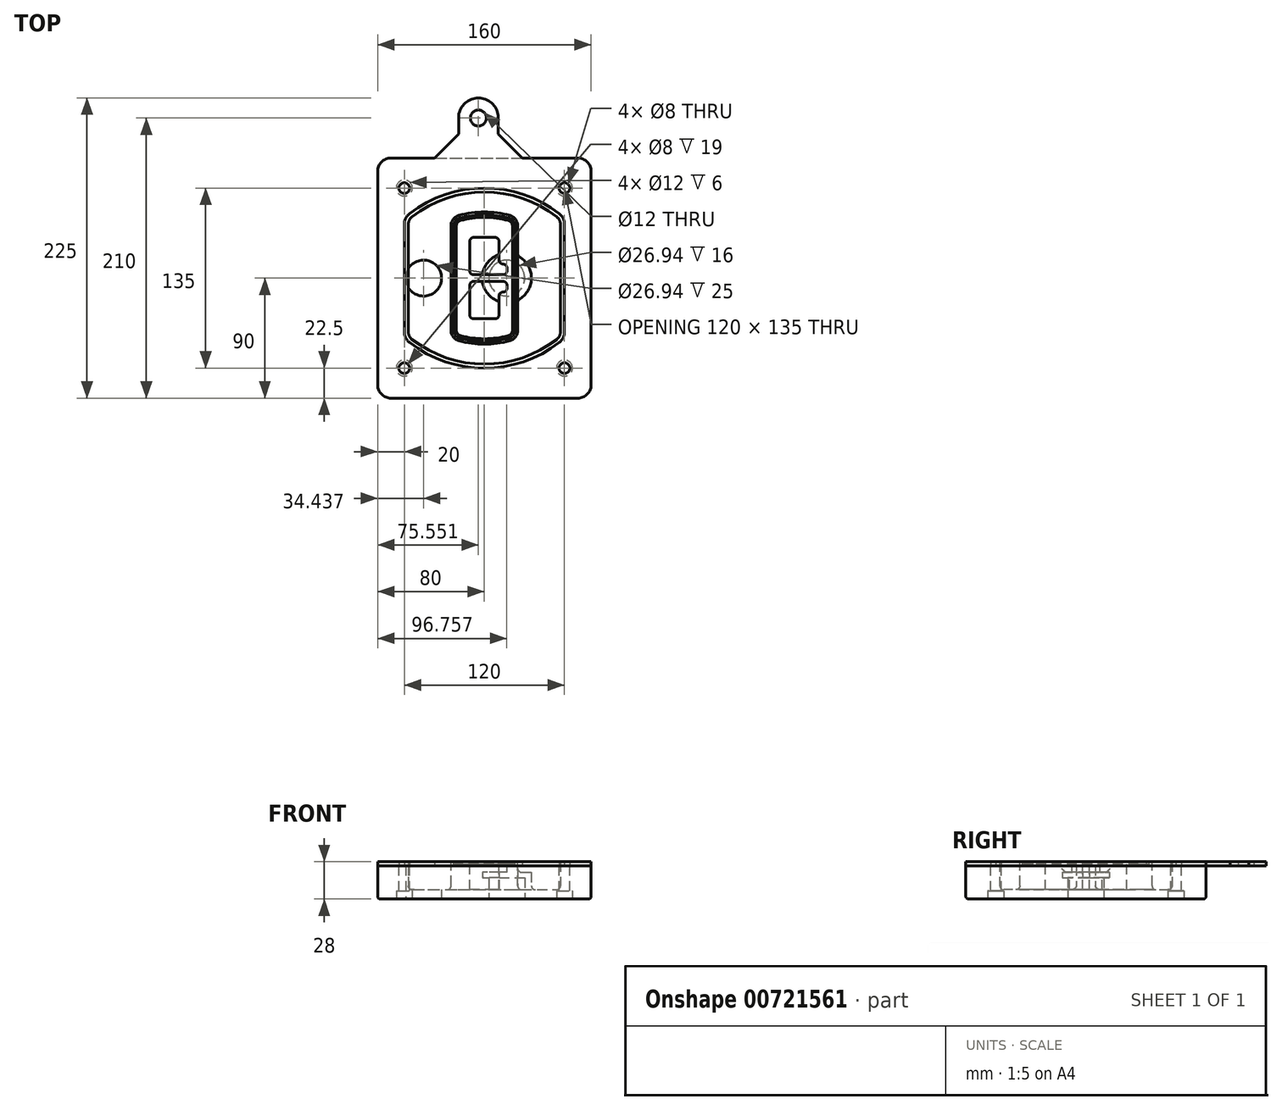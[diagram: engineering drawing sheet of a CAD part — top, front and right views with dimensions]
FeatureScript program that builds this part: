
annotation { "Feature Type Name" : "Feature", "Feature Type Description" : "" }
export const myFeature = defineFeature(function(context is Context, id is Id, definition is map)
    precondition{}
    {
        {
            var Q0;
            Q0=qCreatedBy(makeId("Top.planeOp"),FACE);
            var sketch = newSketch(context, id + "F0", { "sketchPlane" : qUnion([Q0])});
            skPoint(sketch, "E0.rect.middle", {"position": v(0, 0) * mm});
            skLineSegment(sketch, "E1.bottom", {"start": v(-70, -90) * mm, "end": v(70, -90) * mm});
            skLineSegment(sketch, "E1.top", {"start": v(-70, 90) * mm, "end": v(70, 90) * mm});
            skLineSegment(sketch, "E1.left", {"start": v(-80, -80) * mm, "end": v(-80, 80) * mm});
            skLineSegment(sketch, "E1.right", {"start": v(80, -80) * mm, "end": v(80, 80) * mm});
            skLineSegment(sketch, "E2", {"start": v(-80, 90) * mm, "end": v(80, -90) * mm, "construction": true});
            skLineSegment(sketch, "E3", {"start": v(80, 90) * mm, "end": v(-80, -90) * mm, "construction": true});
            skCircle(sketch, "E4", {"center": v(-60, 67.5) * mm, "radius": 4 * mm});
            skCircle(sketch, "E5", {"center": v(60, 67.5) * mm, "radius": 4 * mm});
            skCircle(sketch, "E6", {"center": v(60, -67.5) * mm, "radius": 4 * mm});
            skCircle(sketch, "E7", {"center": v(-60, -67.5) * mm, "radius": 4 * mm});
            skLineSegment(sketch, "E8", {"start": v(-60, 67.5) * mm, "end": v(60, 67.5) * mm, "construction": true});
            skLineSegment(sketch, "E9", {"start": v(60, 67.5) * mm, "end": v(60, -67.5) * mm, "construction": true});
            skLineSegment(sketch, "E10", {"start": v(60, -67.5) * mm, "end": v(-60, -67.5) * mm, "construction": true});
            skLineSegment(sketch, "E11", {"start": v(-60, -67.5) * mm, "end": v(-60, 67.5) * mm, "construction": true});
            skLineSegment(sketch, "E12", {"start": v(-60, 40.3) * mm, "end": v(-60, -40.3) * mm});
            skLineSegment(sketch, "E13", {"start": v(60, 40.3) * mm, "end": v(60, -40.3) * mm});
            skArc(sketch, "E14", {"start": v(56.15, 48.18) * mm, "mid": v(0, 67.5) * mm, "end": v(-56.15, 48.18) * mm});
            skArc(sketch, "E15", {"start": v(-56.15, -48.18) * mm, "mid": v(0, -67.5) * mm, "end": v(56.15, -48.18) * mm});
            skLineSegment(sketch, "E16", {"start": v(-60, 0) * mm, "end": v(60, 0) * mm, "construction": true});
            skPoint(sketch, "E17.visualSharp", {"position": v(-60, -45) * mm});
            skArc(sketch, "E17.filletArc", {"start": v(-60, -40.3) * mm, "mid": v(-58.99, -44.68) * mm, "end": v(-56.15, -48.18) * mm});
            skPoint(sketch, "E18.visualSharp", {"position": v(-60, 45) * mm});
            skArc(sketch, "E18.filletArc", {"start": v(-56.15, 48.18) * mm, "mid": v(-58.99, 44.68) * mm, "end": v(-60, 40.3) * mm});
            skPoint(sketch, "E19.visualSharp", {"position": v(60, 45) * mm});
            skArc(sketch, "E19.filletArc", {"start": v(60, 40.3) * mm, "mid": v(58.99, 44.68) * mm, "end": v(56.15, 48.18) * mm});
            skPoint(sketch, "E20.visualSharp", {"position": v(60, -45) * mm});
            skArc(sketch, "E20.filletArc", {"start": v(56.15, -48.18) * mm, "mid": v(58.99, -44.68) * mm, "end": v(60, -40.3) * mm});
            skPoint(sketch, "E21.visualSharp", {"position": v(-80, 90) * mm});
            skArc(sketch, "E21.filletArc", {"start": v(-70, 90) * mm, "mid": v(-77.07, 87.07) * mm, "end": v(-80, 80) * mm});
            skPoint(sketch, "E22.visualSharp", {"position": v(80, 90) * mm});
            skArc(sketch, "E22.filletArc", {"start": v(80, 80) * mm, "mid": v(77.07, 87.07) * mm, "end": v(70, 90) * mm});
            skPoint(sketch, "E23.visualSharp", {"position": v(80, -90) * mm});
            skArc(sketch, "E23.filletArc", {"start": v(70, -90) * mm, "mid": v(77.07, -87.07) * mm, "end": v(80, -80) * mm});
            skPoint(sketch, "E24.visualSharp", {"position": v(-80, -90) * mm});
            skArc(sketch, "E24.filletArc", {"start": v(-80, -80) * mm, "mid": v(-77.07, -87.07) * mm, "end": v(-70, -90) * mm});
            skArc(sketch, "E25.0", {"start": v(57, 40.3) * mm, "mid": v(56.3, 43.36) * mm, "end": v(54.3, 45.81) * mm});
            skLineSegment(sketch, "E25.1", {"start": v(57, 40.3) * mm, "end": v(57, -40.3) * mm});
            skArc(sketch, "E25.2", {"start": v(54.3, -45.81) * mm, "mid": v(56.3, -43.36) * mm, "end": v(57, -40.3) * mm});
            skArc(sketch, "E25.3", {"start": v(-54.3, -45.81) * mm, "mid": v(0, -64.5) * mm, "end": v(54.3, -45.81) * mm});
            skArc(sketch, "E25.4", {"start": v(-57, -40.3) * mm, "mid": v(-56.3, -43.36) * mm, "end": v(-54.3, -45.81) * mm});
            skArc(sketch, "E25.5", {"start": v(54.3, 45.81) * mm, "mid": v(0, 64.5) * mm, "end": v(-54.3, 45.81) * mm});
            skLineSegment(sketch, "E25.6", {"start": v(-57, 40.3) * mm, "end": v(-57, -40.3) * mm});
            skArc(sketch, "E25.7", {"start": v(-54.3, 45.81) * mm, "mid": v(-56.3, 43.36) * mm, "end": v(-57, 40.3) * mm});
            skArc(sketch, "E26.0", {"start": v(-58.62, 51.33) * mm, "mid": v(-62.58, 46.43) * mm, "end": v(-64, 40.3) * mm});
            skArc(sketch, "E26.1", {"start": v(58.62, 51.33) * mm, "mid": v(0, 71.5) * mm, "end": v(-58.62, 51.33) * mm});
            skArc(sketch, "E26.2", {"start": v(64, 40.3) * mm, "mid": v(62.58, 46.43) * mm, "end": v(58.62, 51.33) * mm});
            skLineSegment(sketch, "E26.3", {"start": v(64, 40.3) * mm, "end": v(64, -40.3) * mm});
            skArc(sketch, "E26.4", {"start": v(58.62, -51.33) * mm, "mid": v(62.58, -46.43) * mm, "end": v(64, -40.3) * mm});
            skLineSegment(sketch, "E26.5", {"start": v(-64, 40.3) * mm, "end": v(-64, -40.3) * mm});
            skArc(sketch, "E26.6", {"start": v(-58.62, -51.33) * mm, "mid": v(0, -71.5) * mm, "end": v(58.62, -51.33) * mm});
            skArc(sketch, "E26.7", {"start": v(-64, -40.3) * mm, "mid": v(-62.58, -46.43) * mm, "end": v(-58.62, -51.33) * mm});
            skSolve(sketch);
        }
        {
            var Q0;
            Q0=makeQuery(id+"F0.imprint","IMPRINT",FACE,{"disambiguationData":[TD([[makeQuery(id+"F0.imprint","IMPRINT",EDGE,{"derivedFrom":sQuery(id+"F0.wireOp",EDGE,"E1.bottom")}),1.0]])]});
            var Q1;
            Q1=makeQuery(id+"F0.imprint","IMPRINT",FACE,{"disambiguationData":[TD([[makeQuery(id+"F0.imprint","IMPRINT",EDGE,{"derivedFrom":sQuery(id+"F0.wireOp",EDGE,"E12")}),1.0]])]});
            var Q2;
            Q2=makeQuery(id+"F0.imprint","IMPRINT",FACE,{"disambiguationData":[TD([[makeQuery(id+"F0.imprint","IMPRINT",EDGE,{"derivedFrom":sQuery(id+"F0.wireOp",EDGE,"E25.0")}),1.0]])]});
            var Q3;
            Q3=makeQuery(id+"F0.imprint","IMPRINT",FACE,{"disambiguationData":[TD([[makeQuery(id+"F0.imprint","IMPRINT",EDGE,{"derivedFrom":sQuery(id+"F0.wireOp",EDGE,"E12")}),-1.0]])]});
            extrude(context, id + "F1", {"entities" : qUnion([Q0, Q1, Q2, Q3]), "oppositeDirection" : true, "depth" : 25 * mm});
        }
        {
            var Q0;
            Q0=makeQuery(id+"F0.imprint","IMPRINT",FACE,{"disambiguationData":[TD([[makeQuery(id+"F0.imprint","IMPRINT",EDGE,{"derivedFrom":sQuery(id+"F0.wireOp",EDGE,"E12")}),1.0]])]});
            extrude(context, id + "F2", {"entities" : qUnion([Q0]), "operationType" : NewBodyOperationType.ADD, "depth" : 3 * mm});
        }
        {
            var Q0;
            Q0=makeQuery(id+"F0.imprint","IMPRINT",FACE,{"disambiguationData":[TD([[makeQuery(id+"F0.imprint","IMPRINT",EDGE,{"derivedFrom":sQuery(id+"F0.wireOp",EDGE,"E25.0")}),1.0]])]});
            extrude(context, id + "F3", {"entities" : qUnion([Q0]), "operationType" : NewBodyOperationType.REMOVE, "oppositeDirection" : true, "depth" : 18 * mm});
        }
        {
            var Q0;
            Q0=makeQuery(id+"F2.opExtrude","CAP_FACE",FACE,{"disambiguationData":[OSD([sQuery(id+"F0.wireOp",EDGE,"E12"),sQuery(id+"F0.wireOp",EDGE,"E13"),sQuery(id+"F0.wireOp",EDGE,"E14"),sQuery(id+"F0.wireOp",EDGE,"E15"),sQuery(id+"F0.wireOp",EDGE,"E17.filletArc"),sQuery(id+"F0.wireOp",EDGE,"E18.filletArc"),sQuery(id+"F0.wireOp",EDGE,"E19.filletArc"),sQuery(id+"F0.wireOp",EDGE,"E20.filletArc"),sQuery(id+"F0.wireOp",EDGE,"E25.0"),sQuery(id+"F0.wireOp",EDGE,"E25.1"),sQuery(id+"F0.wireOp",EDGE,"E25.2"),sQuery(id+"F0.wireOp",EDGE,"E25.3"),sQuery(id+"F0.wireOp",EDGE,"E25.4"),sQuery(id+"F0.wireOp",EDGE,"E25.5"),sQuery(id+"F0.wireOp",EDGE,"E25.6"),sQuery(id+"F0.wireOp",EDGE,"E25.7")])],"isStart":false});
            var sketch = newSketch(context, id + "F4", { "sketchPlane" : qUnion([Q0])});
            skArc(sketch, "E27.0", {"start": v(-19.08, -46.97) * mm, "mid": v(0, -49.5) * mm, "end": v(19.08, -46.97) * mm});
            skArc(sketch, "E28.0", {"start": v(19.08, 46.97) * mm, "mid": v(0, 49.5) * mm, "end": v(-19.08, 46.97) * mm});
            skLineSegment(sketch, "E29", {"start": v(-25, 39.25) * mm, "end": v(-25, -39.25) * mm});
            skLineSegment(sketch, "E30", {"start": v(25, 39.25) * mm, "end": v(25, -39.25) * mm});
            skLineSegment(sketch, "E31", {"start": v(-25, 45.1) * mm, "end": v(25, 45.1) * mm, "construction": true});
            skLineSegment(sketch, "E32", {"start": v(-25, -45.1) * mm, "end": v(25, -45.1) * mm, "construction": true});
            skPoint(sketch, "E33.visualSharp", {"position": v(-25, 45.1) * mm});
            skArc(sketch, "E33.filletArc", {"start": v(-19.08, 46.97) * mm, "mid": v(-23.35, 44.11) * mm, "end": v(-25, 39.25) * mm});
            skPoint(sketch, "E34.visualSharp", {"position": v(25, 45.1) * mm});
            skArc(sketch, "E34.filletArc", {"start": v(25, 39.25) * mm, "mid": v(23.35, 44.11) * mm, "end": v(19.08, 46.97) * mm});
            skPoint(sketch, "E35.visualSharp", {"position": v(25, -45.1) * mm});
            skArc(sketch, "E35.filletArc", {"start": v(19.08, -46.97) * mm, "mid": v(23.35, -44.11) * mm, "end": v(25, -39.25) * mm});
            skPoint(sketch, "E36.visualSharp", {"position": v(-25, -45.1) * mm});
            skArc(sketch, "E36.filletArc", {"start": v(-25, -39.25) * mm, "mid": v(-23.35, -44.11) * mm, "end": v(-19.08, -46.97) * mm});
            skArc(sketch, "E37.0", {"start": v(54.3, 45.81) * mm, "mid": v(0, 64.5) * mm, "end": v(-54.3, 45.81) * mm});
            skArc(sketch, "E37.1", {"start": v(-54.3, 45.81) * mm, "mid": v(-56.3, 43.36) * mm, "end": v(-57, 40.3) * mm});
            skLineSegment(sketch, "E37.2", {"start": v(-57, 40.3) * mm, "end": v(-57, -40.3) * mm});
            skArc(sketch, "E37.3", {"start": v(-57, -40.3) * mm, "mid": v(-56.3, -43.36) * mm, "end": v(-54.3, -45.81) * mm});
            skArc(sketch, "E37.4", {"start": v(-54.3, -45.81) * mm, "mid": v(0, -64.5) * mm, "end": v(54.3, -45.81) * mm});
            skArc(sketch, "E37.5", {"start": v(54.3, -45.81) * mm, "mid": v(56.3, -43.36) * mm, "end": v(57, -40.3) * mm});
            skLineSegment(sketch, "E37.6", {"start": v(57, 40.3) * mm, "end": v(57, -40.3) * mm});
            skArc(sketch, "E37.7", {"start": v(57, 40.3) * mm, "mid": v(56.3, 43.36) * mm, "end": v(54.3, 45.81) * mm});
            skLineSegment(sketch, "E38.0", {"start": v(23, 39.25) * mm, "end": v(23, -39.25) * mm});
            skArc(sketch, "E38.1", {"start": v(18.56, -45.04) * mm, "mid": v(21.76, -42.9) * mm, "end": v(23, -39.25) * mm});
            skArc(sketch, "E38.2", {"start": v(-18.56, -45.04) * mm, "mid": v(0, -47.5) * mm, "end": v(18.56, -45.04) * mm});
            skArc(sketch, "E38.3", {"start": v(-23, -39.25) * mm, "mid": v(-21.76, -42.9) * mm, "end": v(-18.56, -45.04) * mm});
            skLineSegment(sketch, "E38.4", {"start": v(-23, 39.25) * mm, "end": v(-23, -39.25) * mm});
            skArc(sketch, "E38.5", {"start": v(23, 39.25) * mm, "mid": v(21.76, 42.9) * mm, "end": v(18.56, 45.04) * mm});
            skArc(sketch, "E38.6", {"start": v(-18.56, 45.04) * mm, "mid": v(-21.76, 42.9) * mm, "end": v(-23, 39.25) * mm});
            skArc(sketch, "E38.7", {"start": v(18.56, 45.04) * mm, "mid": v(0, 47.5) * mm, "end": v(-18.56, 45.04) * mm});
            skArc(sketch, "E39.0", {"start": v(21, 39.25) * mm, "mid": v(20.18, 41.68) * mm, "end": v(18.04, 43.1) * mm});
            skLineSegment(sketch, "E39.1", {"start": v(21, 39.25) * mm, "end": v(21, -39.25) * mm});
            skArc(sketch, "E39.2", {"start": v(18.04, -43.1) * mm, "mid": v(20.18, -41.68) * mm, "end": v(21, -39.25) * mm});
            skArc(sketch, "E39.3", {"start": v(-18.04, -43.1) * mm, "mid": v(0, -45.5) * mm, "end": v(18.04, -43.1) * mm});
            skArc(sketch, "E39.4", {"start": v(-21, -39.25) * mm, "mid": v(-20.18, -41.68) * mm, "end": v(-18.04, -43.1) * mm});
            skArc(sketch, "E39.5", {"start": v(18.04, 43.1) * mm, "mid": v(0, 45.5) * mm, "end": v(-18.04, 43.1) * mm});
            skLineSegment(sketch, "E39.6", {"start": v(-21, 39.25) * mm, "end": v(-21, -39.25) * mm});
            skArc(sketch, "E39.7", {"start": v(-18.04, 43.1) * mm, "mid": v(-20.18, 41.68) * mm, "end": v(-21, 39.25) * mm});
            skLineSegment(sketch, "E40", {"start": v(-25, 0) * mm, "end": v(25, 0) * mm, "construction": true});
            skLineSegment(sketch, "E41", {"start": v(-11, 5.5) * mm, "end": v(-11, 27.5) * mm});
            skLineSegment(sketch, "E42", {"start": v(-8, 30.5) * mm, "end": v(8, 30.5) * mm});
            skLineSegment(sketch, "E43", {"start": v(11, 27.5) * mm, "end": v(11, 13.5) * mm});
            skLineSegment(sketch, "E44", {"start": v(14, 10.5) * mm, "end": v(14, 10.5) * mm});
            skLineSegment(sketch, "E45", {"start": v(17, 7.5) * mm, "end": v(17, 5.5) * mm});
            skLineSegment(sketch, "E46", {"start": v(14, 2.5) * mm, "end": v(-8, 2.5) * mm});
            skPoint(sketch, "E47.visualSharp", {"position": v(-11, 30.5) * mm});
            skArc(sketch, "E47.filletArc", {"start": v(-8, 30.5) * mm, "mid": v(-10.12, 29.62) * mm, "end": v(-11, 27.5) * mm});
            skPoint(sketch, "E48.visualSharp", {"position": v(11, 30.5) * mm});
            skArc(sketch, "E48.filletArc", {"start": v(11, 27.5) * mm, "mid": v(10.12, 29.62) * mm, "end": v(8, 30.5) * mm});
            skPoint(sketch, "E49.visualSharp", {"position": v(11, 10.5) * mm});
            skArc(sketch, "E49.filletArc", {"start": v(11, 13.5) * mm, "mid": v(11.88, 11.38) * mm, "end": v(14, 10.5) * mm});
            skPoint(sketch, "E50.visualSharp", {"position": v(17, 10.5) * mm});
            skArc(sketch, "E50.filletArc", {"start": v(17, 7.5) * mm, "mid": v(16.12, 9.62) * mm, "end": v(14, 10.5) * mm});
            skPoint(sketch, "E51.visualSharp", {"position": v(17, 2.5) * mm});
            skArc(sketch, "E51.filletArc", {"start": v(14, 2.5) * mm, "mid": v(16.12, 3.38) * mm, "end": v(17, 5.5) * mm});
            skPoint(sketch, "E52.visualSharp", {"position": v(-11, 2.5) * mm});
            skArc(sketch, "E52.filletArc", {"start": v(-11, 5.5) * mm, "mid": v(-10.12, 3.38) * mm, "end": v(-8, 2.5) * mm});
            skLineSegment(sketch, "E53.0.MirrorCS", {"start": v(14, -2.5) * mm, "end": v(-8, -2.5) * mm});
            skArc(sketch, "E54.0.MirrorCS", {"start": v(-11, -5.5) * mm, "mid": v(-10.12, -3.38) * mm, "end": v(-8, -2.5) * mm});
            skLineSegment(sketch, "E55.0.MirrorCS", {"start": v(-11, -5.5) * mm, "end": v(-11, -27.5) * mm});
            skArc(sketch, "E56.0.MirrorCS", {"start": v(-8, -30.5) * mm, "mid": v(-10.12, -29.62) * mm, "end": v(-11, -27.5) * mm});
            skLineSegment(sketch, "E57.0.MirrorCS", {"start": v(-8, -30.5) * mm, "end": v(8, -30.5) * mm});
            skArc(sketch, "E58.0.MirrorCS", {"start": v(11, -27.5) * mm, "mid": v(10.12, -29.62) * mm, "end": v(8, -30.5) * mm});
            skLineSegment(sketch, "E59.0.MirrorCS", {"start": v(11, -27.5) * mm, "end": v(11, -13.5) * mm});
            skArc(sketch, "E60.0.MirrorCS", {"start": v(11, -13.5) * mm, "mid": v(11.88, -11.38) * mm, "end": v(14, -10.5) * mm});
            skArc(sketch, "E61.0.MirrorCS", {"start": v(17, -7.5) * mm, "mid": v(16.12, -9.62) * mm, "end": v(14, -10.5) * mm});
            skLineSegment(sketch, "E62.0.MirrorCS", {"start": v(17, -7.5) * mm, "end": v(17, -5.5) * mm});
            skArc(sketch, "E63.0.MirrorCS", {"start": v(14, -2.5) * mm, "mid": v(16.12, -3.38) * mm, "end": v(17, -5.5) * mm});
            skSolve(sketch);
        }
        {
            var Q0;
            Q0=makeQuery(id+"F4.imprint","IMPRINT",FACE,{"disambiguationData":[TD([[makeQuery(id+"F4.imprint","IMPRINT",EDGE,{"derivedFrom":sQuery(id+"F4.wireOp",EDGE,"E27.0")}),1.0]])]});
            var Q1;
            Q1=makeQuery(id+"F4.imprint","IMPRINT",FACE,{"disambiguationData":[TD([[makeQuery(id+"F4.imprint","IMPRINT",EDGE,{"derivedFrom":sQuery(id+"F4.wireOp",EDGE,"E38.0")}),-1.0]])]});
            var Q2;
            Q2=makeQuery(id+"F4.imprint","IMPRINT",FACE,{"disambiguationData":[TD([[makeQuery(id+"F4.imprint","IMPRINT",EDGE,{"derivedFrom":sQuery(id+"F4.wireOp",EDGE,"E39.0")}),1.0]])]});
            extrude(context, id + "F5", {"entities" : qUnion([Q0, Q1, Q2]), "operationType" : NewBodyOperationType.ADD, "endBound" : BoundingType.UP_TO_NEXT, "oppositeDirection" : true, "depth" : 25 * mm});
        }
        {
            var Q0;
            Q0=makeQuery(id+"F4.imprint","IMPRINT",FACE,{"disambiguationData":[TD([[makeQuery(id+"F4.imprint","IMPRINT",EDGE,{"derivedFrom":sQuery(id+"F4.wireOp",EDGE,"E38.0")}),-1.0]])]});
            extrude(context, id + "F6", {"entities" : qUnion([Q0]), "operationType" : NewBodyOperationType.REMOVE, "oppositeDirection" : true, "depth" : 2 * mm});
        }
        {
            var Q0;
            Q0=makeQuery(id+"F1.opExtrude","CAP_FACE",FACE,{"disambiguationData":[OSD([sQuery(id+"F0.wireOp",EDGE,"E1.bottom"),sQuery(id+"F0.wireOp",EDGE,"E1.top"),sQuery(id+"F0.wireOp",EDGE,"E1.left"),sQuery(id+"F0.wireOp",EDGE,"E1.right"),sQuery(id+"F0.wireOp",EDGE,"E4"),sQuery(id+"F0.wireOp",EDGE,"E5"),sQuery(id+"F0.wireOp",EDGE,"E6"),sQuery(id+"F0.wireOp",EDGE,"E7"),sQuery(id+"F0.wireOp",EDGE,"E21.filletArc"),sQuery(id+"F0.wireOp",EDGE,"E22.filletArc"),sQuery(id+"F0.wireOp",EDGE,"E23.filletArc"),sQuery(id+"F0.wireOp",EDGE,"E24.filletArc")])],"isStart":false});
            var sketch = newSketch(context, id + "F7", { "sketchPlane" : qUnion([Q0])});
            skCircle(sketch, "E64", {"center": v(16.76, 0) * mm, "radius": 13.47 * mm});
            skCircle(sketch, "E65", {"center": v(-45.56, 0) * mm, "radius": 13.47 * mm});
            skLineSegment(sketch, "E66", {"start": v(80, 0) * mm, "end": v(-80, 0) * mm});
            skCircle(sketch, "E67", {"center": v(16.76, 0) * mm, "radius": 18.47 * mm});
            skCircle(sketch, "E68", {"center": v(60, -67.5) * mm, "radius": 6 * mm});
            skCircle(sketch, "E69", {"center": v(-60, -67.5) * mm, "radius": 6 * mm});
            skCircle(sketch, "E70", {"center": v(-60, 67.5) * mm, "radius": 6 * mm});
            skCircle(sketch, "E71", {"center": v(60, 67.5) * mm, "radius": 6 * mm});
            skSolve(sketch);
        }
        {
            var Q0;
            {var subQ1=sQuery(id+"F7.wireOp",EDGE,"E66");var subQ4=sQuery(id+"F7.wireOp",EDGE,"E64");var subQ6=makeQuery(id+"F7.imprint","INTERSECT",VERTEX,{"disambiguationData":[OD(0.0)],"derivedFrom":[subQ4,subQ1]});Q0=makeQuery(id+"F7.imprint","IMPRINT",FACE,{"disambiguationData":[TD([[makeQuery(id+"F7.imprint","IMPRINT",EDGE,{"disambiguationData":[TD([[subQ6,-1.0]])],"derivedFrom":subQ4}),-1.0]])]});}
            var Q1;
            {var subQ0=sQuery(id+"F7.wireOp",EDGE,"E66");var subQ1=sQuery(id+"F7.wireOp",EDGE,"E64");var subQ3=makeQuery(id+"F7.imprint","INTERSECT",VERTEX,{"disambiguationData":[OD(0.0)],"derivedFrom":[subQ1,subQ0]});Q1=makeQuery(id+"F7.imprint","IMPRINT",FACE,{"disambiguationData":[TD([[makeQuery(id+"F7.imprint","IMPRINT",EDGE,{"disambiguationData":[TD([[subQ3,-1.0]])],"derivedFrom":subQ1}),1.0]])]});}
            var Q2;
            {var subQ0=sQuery(id+"F7.wireOp",EDGE,"E66");var subQ1=sQuery(id+"F7.wireOp",EDGE,"E64");var subQ3=makeQuery(id+"F7.imprint","INTERSECT",VERTEX,{"disambiguationData":[OD(0.0)],"derivedFrom":[subQ1,subQ0]});Q2=makeQuery(id+"F7.imprint","IMPRINT",FACE,{"disambiguationData":[TD([[makeQuery(id+"F7.imprint","IMPRINT",EDGE,{"disambiguationData":[TD([[subQ3,1.0]])],"derivedFrom":subQ1}),1.0]])]});}
            var Q3;
            {var subQ1=sQuery(id+"F7.wireOp",EDGE,"E66");var subQ4=sQuery(id+"F7.wireOp",EDGE,"E64");var subQ6=makeQuery(id+"F7.imprint","INTERSECT",VERTEX,{"disambiguationData":[OD(0.0)],"derivedFrom":[subQ4,subQ1]});Q3=makeQuery(id+"F7.imprint","IMPRINT",FACE,{"disambiguationData":[TD([[makeQuery(id+"F7.imprint","IMPRINT",EDGE,{"disambiguationData":[TD([[subQ6,1.0]])],"derivedFrom":subQ4}),-1.0]])]});}
            extrude(context, id + "F8", {"entities" : qUnion([Q0, Q1, Q2, Q3]), "operationType" : NewBodyOperationType.ADD, "oppositeDirection" : true, "depth" : 20 * mm});
        }
        {
            var Q0;
            {var subQ0=sQuery(id+"F7.wireOp",EDGE,"E66");var subQ1=sQuery(id+"F7.wireOp",EDGE,"E64");var subQ3=makeQuery(id+"F7.imprint","INTERSECT",VERTEX,{"disambiguationData":[OD(0.0)],"derivedFrom":[subQ1,subQ0]});Q0=makeQuery(id+"F7.imprint","IMPRINT",FACE,{"disambiguationData":[TD([[makeQuery(id+"F7.imprint","IMPRINT",EDGE,{"disambiguationData":[TD([[subQ3,-1.0]])],"derivedFrom":subQ1}),1.0]])]});}
            var Q1;
            {var subQ0=sQuery(id+"F7.wireOp",EDGE,"E66");var subQ1=sQuery(id+"F7.wireOp",EDGE,"E64");var subQ3=makeQuery(id+"F7.imprint","INTERSECT",VERTEX,{"disambiguationData":[OD(0.0)],"derivedFrom":[subQ1,subQ0]});Q1=makeQuery(id+"F7.imprint","IMPRINT",FACE,{"disambiguationData":[TD([[makeQuery(id+"F7.imprint","IMPRINT",EDGE,{"disambiguationData":[TD([[subQ3,1.0]])],"derivedFrom":subQ1}),1.0]])]});}
            extrude(context, id + "F9", {"entities" : qUnion([Q0, Q1]), "operationType" : NewBodyOperationType.REMOVE, "oppositeDirection" : true, "depth" : 16 * mm});
        }
        {
            var Q0;
            {var subQ0=sQuery(id+"F7.wireOp",EDGE,"E66");var subQ1=sQuery(id+"F7.wireOp",EDGE,"E65");var subQ3=makeQuery(id+"F7.imprint","INTERSECT",VERTEX,{"disambiguationData":[OD(0.0)],"derivedFrom":[subQ1,subQ0]});Q0=makeQuery(id+"F7.imprint","IMPRINT",FACE,{"disambiguationData":[TD([[makeQuery(id+"F7.imprint","IMPRINT",EDGE,{"disambiguationData":[TD([[subQ3,-1.0]])],"derivedFrom":subQ1}),1.0]])]});}
            var Q1;
            {var subQ0=sQuery(id+"F7.wireOp",EDGE,"E66");var subQ1=sQuery(id+"F7.wireOp",EDGE,"E65");var subQ3=makeQuery(id+"F7.imprint","INTERSECT",VERTEX,{"disambiguationData":[OD(0.0)],"derivedFrom":[subQ1,subQ0]});Q1=makeQuery(id+"F7.imprint","IMPRINT",FACE,{"disambiguationData":[TD([[makeQuery(id+"F7.imprint","IMPRINT",EDGE,{"disambiguationData":[TD([[subQ3,1.0]])],"derivedFrom":subQ1}),1.0]])]});}
            extrude(context, id + "F10", {"entities" : qUnion([Q0, Q1]), "operationType" : NewBodyOperationType.REMOVE, "oppositeDirection" : true, "depth" : 25 * mm});
        }
        {
            var Q0;
            Q0=makeQuery(id+"F7.imprint","IMPRINT",FACE,{"disambiguationData":[TD([[makeQuery(id+"F7.imprint","IMPRINT",EDGE,{"derivedFrom":sQuery(id+"F7.wireOp",EDGE,"E68")}),1.0]])]});
            var Q1;
            Q1=makeQuery(id+"F7.imprint","IMPRINT",FACE,{"disambiguationData":[TD([[makeQuery(id+"F7.imprint","IMPRINT",EDGE,{"derivedFrom":makeQuery(id+"F1.opExtrude","CAP_EDGE",EDGE,{"disambiguationData":[OSD([sQuery(id+"F0.wireOp",EDGE,"E5")])],"isStart":false})}),-1.0]])]});
            var Q2;
            Q2=makeQuery(id+"F7.imprint","IMPRINT",FACE,{"disambiguationData":[TD([[makeQuery(id+"F7.imprint","IMPRINT",EDGE,{"derivedFrom":sQuery(id+"F7.wireOp",EDGE,"E69")}),1.0]])]});
            var Q3;
            Q3=makeQuery(id+"F7.imprint","IMPRINT",FACE,{"disambiguationData":[TD([[makeQuery(id+"F7.imprint","IMPRINT",EDGE,{"derivedFrom":makeQuery(id+"F1.opExtrude","CAP_EDGE",EDGE,{"disambiguationData":[OSD([sQuery(id+"F0.wireOp",EDGE,"E4")])],"isStart":false})}),-1.0]])]});
            var Q4;
            Q4=makeQuery(id+"F7.imprint","IMPRINT",FACE,{"disambiguationData":[TD([[makeQuery(id+"F7.imprint","IMPRINT",EDGE,{"derivedFrom":sQuery(id+"F7.wireOp",EDGE,"E70")}),1.0]])]});
            var Q5;
            Q5=makeQuery(id+"F7.imprint","IMPRINT",FACE,{"disambiguationData":[TD([[makeQuery(id+"F7.imprint","IMPRINT",EDGE,{"derivedFrom":makeQuery(id+"F1.opExtrude","CAP_EDGE",EDGE,{"disambiguationData":[OSD([sQuery(id+"F0.wireOp",EDGE,"E7")])],"isStart":false})}),-1.0]])]});
            var Q6;
            Q6=makeQuery(id+"F7.imprint","IMPRINT",FACE,{"disambiguationData":[TD([[makeQuery(id+"F7.imprint","IMPRINT",EDGE,{"derivedFrom":sQuery(id+"F7.wireOp",EDGE,"E71")}),1.0]])]});
            var Q7;
            Q7=makeQuery(id+"F7.imprint","IMPRINT",FACE,{"disambiguationData":[TD([[makeQuery(id+"F7.imprint","IMPRINT",EDGE,{"derivedFrom":makeQuery(id+"F1.opExtrude","CAP_EDGE",EDGE,{"disambiguationData":[OSD([sQuery(id+"F0.wireOp",EDGE,"E6")])],"isStart":false})}),-1.0]])]});
            extrude(context, id + "F11", {"entities" : qUnion([Q0, Q1, Q2, Q3, Q4, Q5, Q6, Q7]), "operationType" : NewBodyOperationType.REMOVE, "oppositeDirection" : true, "depth" : 6 * mm});
        }
        {
            var Q0;
            Q0=makeQuery(id+"F9.boolean.opBoolean","COPY",FACE,{"derivedFrom":makeQuery(id+"F9.opExtrude","CAP_FACE",FACE,{"disambiguationData":[OSD([sQuery(id+"F7.wireOp",EDGE,"E64")])],"isStart":false})});
            var sketch = newSketch(context, id + "F12", { "sketchPlane" : qUnion([Q0])});
            skArc(sketch, "E72.0", {"start": v(11, 17.55) * mm, "mid": v(2.57, 11.82) * mm, "end": v(-1.54, 2.5) * mm});
            skArc(sketch, "E72.1", {"start": v(-1.54, -2.5) * mm, "mid": v(2.57, -11.82) * mm, "end": v(11, -17.55) * mm});
            skLineSegment(sketch, "E73", {"start": v(-1.54, -2.5) * mm, "end": v(14, -2.5) * mm});
            skLineSegment(sketch, "E74.0", {"start": v(14, 2.5) * mm, "end": v(-1.54, 2.5) * mm});
            skArc(sketch, "E74.1", {"start": v(14, 2.5) * mm, "mid": v(16.12, 3.38) * mm, "end": v(17, 5.5) * mm});
            skLineSegment(sketch, "E74.2", {"start": v(17, 7.5) * mm, "end": v(17, 5.5) * mm});
            skArc(sketch, "E74.3", {"start": v(17, 7.5) * mm, "mid": v(16.12, 9.62) * mm, "end": v(14, 10.5) * mm});
            skArc(sketch, "E74.4", {"start": v(11, 13.5) * mm, "mid": v(11.88, 11.38) * mm, "end": v(14, 10.5) * mm});
            skLineSegment(sketch, "E74.5", {"start": v(11, 17.55) * mm, "end": v(11, 13.5) * mm});
            skLineSegment(sketch, "E74.7", {"start": v(14, -2.5) * mm, "end": v(-1.54, -2.5) * mm});
            skArc(sketch, "E74.8", {"start": v(14, -2.5) * mm, "mid": v(16.12, -3.38) * mm, "end": v(17, -5.5) * mm});
            skLineSegment(sketch, "E74.9", {"start": v(17, -7.5) * mm, "end": v(17, -5.5) * mm});
            skArc(sketch, "E74.10", {"start": v(17, -7.5) * mm, "mid": v(16.12, -9.62) * mm, "end": v(14, -10.5) * mm});
            skArc(sketch, "E74.11", {"start": v(11, -13.5) * mm, "mid": v(11.88, -11.38) * mm, "end": v(14, -10.5) * mm});
            skLineSegment(sketch, "E74.12", {"start": v(11, -17.55) * mm, "end": v(11, -13.5) * mm});
            skPoint(sketch, "E75.orphan", {"position": v(11, -27.5) * mm});
            skPoint(sketch, "E76.orphan", {"position": v(-8, -2.5) * mm});
            skPoint(sketch, "E77.orphan", {"position": v(-8, 2.5) * mm});
            skPoint(sketch, "E78.orphan", {"position": v(11, 27.5) * mm});
            skSolve(sketch);
        }
        {
            var Q0;
            {var subQ7=sQuery(id+"F12.wireOp",EDGE,"E72.0");var subQ14=sQuery(id+"F12.wireOp",EDGE,"E72.1");var subQ16=sQuery(id+"F12.wireOp",EDGE,"E74.1");var subQ18=sQuery(id+"F12.wireOp",EDGE,"E74.8");Q0=qUnion([makeQuery(id+"F12.imprint","IMPRINT",FACE,{"disambiguationData":[TD([[makeQuery(id+"F12.imprint","IMPRINT",EDGE,{"derivedFrom":subQ7}),1.0]])]}),makeQuery(id+"F12.imprint","IMPRINT",FACE,{"disambiguationData":[TD([[makeQuery(id+"F12.imprint","IMPRINT",EDGE,{"derivedFrom":subQ14}),1.0]])]}),makeQuery(id+"F12.imprint","IMPRINT",FACE,{"disambiguationData":[TD([[makeQuery(id+"F12.imprint","IMPRINT",EDGE,{"derivedFrom":subQ16}),1.0]])]}),makeQuery(id+"F12.imprint","IMPRINT",FACE,{"disambiguationData":[TD([[makeQuery(id+"F12.imprint","IMPRINT",EDGE,{"derivedFrom":subQ18}),-1.0]])]})]);}
            var Q1;
            Q1=makeQuery(id+"F5.boolean.opBoolean","SPLIT",FACE,{"disambiguationData":[TD([makeQuery(id+"F5.opExtrude","SWEPT_FACE",FACE,{"disambiguationData":[OSD([sQuery(id+"F4.wireOp",EDGE,"E41")])]})])],"derivedFrom":makeQuery(id+"F3.boolean.opBoolean","COPY",FACE,{"derivedFrom":makeQuery(id+"F3.opExtrude","CAP_FACE",FACE,{"disambiguationData":[OSD([sQuery(id+"F0.wireOp",EDGE,"E25.0"),sQuery(id+"F0.wireOp",EDGE,"E25.1"),sQuery(id+"F0.wireOp",EDGE,"E25.2"),sQuery(id+"F0.wireOp",EDGE,"E25.3"),sQuery(id+"F0.wireOp",EDGE,"E25.4"),sQuery(id+"F0.wireOp",EDGE,"E25.5"),sQuery(id+"F0.wireOp",EDGE,"E25.6"),sQuery(id+"F0.wireOp",EDGE,"E25.7")])],"isStart":false})})});
            extrude(context, id + "F13", {"entities" : qUnion([Q0]), "operationType" : NewBodyOperationType.REMOVE, "endBound" : BoundingType.UP_TO_SURFACE, "endBoundEntityFace" : qUnion([Q1]), "depth" : 25 * mm});
        }
        {
            var Q0;
            Q0=makeQuery(id+"F3.boolean.opBoolean","COPY",EDGE,{"derivedFrom":makeQuery(id+"F3.opExtrude","CAP_EDGE",EDGE,{"disambiguationData":[OSD([sQuery(id+"F0.wireOp",EDGE,"E25.6")])],"isStart":false})});
            var Q1;
            Q1=makeQuery(id+"F8.boolean.opBoolean","INTERSECT",EDGE,{"derivedFrom":[makeQuery(id+"F5.opExtrude","SWEPT_FACE",FACE,{"disambiguationData":[OSD([sQuery(id+"F4.wireOp",EDGE,"E30")])]}),makeQuery(id+"F8.opExtrude","CAP_FACE",FACE,{"disambiguationData":[OSD([sQuery(id+"F7.wireOp",EDGE,"E67")])],"isStart":false})]});
            var Q2;
            Q2=makeQuery(id+"F8.boolean.opBoolean","INTERSECT",EDGE,{"disambiguationData":[OD(1.0)],"derivedFrom":[makeQuery(id+"F5.opExtrude","SWEPT_FACE",FACE,{"disambiguationData":[OSD([sQuery(id+"F4.wireOp",EDGE,"E30")])]}),makeQuery(id+"F8.opExtrude","SWEPT_FACE",FACE,{"disambiguationData":[OSD([sQuery(id+"F7.wireOp",EDGE,"E67")])]})]});
            var Q3;
            {var subQ0=sQuery(id+"F4.wireOp",EDGE,"E30");Q3=makeQuery(id+"F8.boolean.opBoolean","SPLIT",EDGE,{"disambiguationData":[TD([makeQuery(id+"F5.opExtrude","SWEPT_FACE",FACE,{"disambiguationData":[OSD([sQuery(id+"F4.wireOp",EDGE,"E35.filletArc")])]})])],"derivedFrom":makeQuery(id+"F5.opExtrude","CAP_EDGE",EDGE,{"disambiguationData":[OSD([subQ0])],"isStart":false})});}
            var Q4;
            {var subQ0=sQuery(id+"F0.wireOp",EDGE,"E25.7");var subQ1=sQuery(id+"F0.wireOp",EDGE,"E25.1");var subQ2=sQuery(id+"F0.wireOp",EDGE,"E25.6");var subQ3=sQuery(id+"F0.wireOp",EDGE,"E25.5");var subQ4=sQuery(id+"F0.wireOp",EDGE,"E25.4");var subQ5=sQuery(id+"F0.wireOp",EDGE,"E25.0");var subQ6=sQuery(id+"F0.wireOp",EDGE,"E25.2");var subQ7=sQuery(id+"F0.wireOp",EDGE,"E25.3");Q4=makeQuery(id+"F8.boolean.opBoolean","INTERSECT",EDGE,{"derivedFrom":[makeQuery(id+"F5.boolean.opBoolean","SPLIT",FACE,{"disambiguationData":[TD([makeQuery(id+"F2.opExtrude","SWEPT_FACE",FACE,{"disambiguationData":[OSD([subQ5])]})])],"derivedFrom":makeQuery(id+"F3.boolean.opBoolean","COPY",FACE,{"derivedFrom":makeQuery(id+"F3.opExtrude","CAP_FACE",FACE,{"disambiguationData":[OSD([subQ5,subQ1,subQ6,subQ7,subQ4,subQ3,subQ2,subQ0])],"isStart":false})})}),makeQuery(id+"F8.opExtrude","SWEPT_FACE",FACE,{"disambiguationData":[OSD([sQuery(id+"F7.wireOp",EDGE,"E67")])]})]});}
            var Q5;
            Q5=makeQuery(id+"F8.boolean.opBoolean","INTERSECT",EDGE,{"disambiguationData":[OD(0.0)],"derivedFrom":[makeQuery(id+"F5.opExtrude","SWEPT_FACE",FACE,{"disambiguationData":[OSD([sQuery(id+"F4.wireOp",EDGE,"E30")])]}),makeQuery(id+"F8.opExtrude","SWEPT_FACE",FACE,{"disambiguationData":[OSD([sQuery(id+"F7.wireOp",EDGE,"E67")])]})]});
            fillet(context, id + "F14", {"entities" : qUnion([Q0, Q1, Q2, Q3, Q4, Q5]), "radius" : 3 * mm, "tangentPropagation" : true, "allowEdgeOverflow" : false});
        }
        {
            var Q0;
            Q0=makeQuery(id+"F1.opExtrude","CAP_EDGE",EDGE,{"disambiguationData":[OSD([sQuery(id+"F0.wireOp",EDGE,"E1.bottom")])],"isStart":false});
            fillet(context, id + "F15", {"entities" : qUnion([Q0]), "radius" : 2 * mm, "tangentPropagation" : true, "allowEdgeOverflow" : false});
        }
        {
            var Q0;
            {var subQ0=sQuery(id+"F0.wireOp",EDGE,"E21.filletArc");var subQ1=sQuery(id+"F0.wireOp",EDGE,"E7");var subQ2=sQuery(id+"F0.wireOp",EDGE,"E6");var subQ3=sQuery(id+"F0.wireOp",EDGE,"E5");var subQ4=sQuery(id+"F0.wireOp",EDGE,"E4");var subQ5=sQuery(id+"F0.wireOp",EDGE,"E22.filletArc");var subQ6=sQuery(id+"F0.wireOp",EDGE,"E1.bottom");var subQ7=sQuery(id+"F0.wireOp",EDGE,"E1.right");var subQ8=sQuery(id+"F0.wireOp",EDGE,"E1.top");var subQ9=sQuery(id+"F0.wireOp",EDGE,"E1.left");var subQ10=sQuery(id+"F0.wireOp",EDGE,"E23.filletArc");var subQ11=sQuery(id+"F0.wireOp",EDGE,"E24.filletArc");Q0=makeQuery(id+"F2.boolean.opBoolean","SPLIT",FACE,{"disambiguationData":[TD([makeQuery(id+"F1.opExtrude","SWEPT_FACE",FACE,{"disambiguationData":[OSD([subQ6])]})])],"derivedFrom":makeQuery(id+"F1.opExtrude","CAP_FACE",FACE,{"disambiguationData":[OSD([subQ6,subQ8,subQ9,subQ7,subQ4,subQ3,subQ2,subQ1,subQ0,subQ5,subQ10,subQ11])],"isStart":true})});}
            var sketch = newSketch(context, id + "F16", { "sketchPlane" : qUnion([Q0])});
            skLineSegment(sketch, "E79", {"start": v(-37.32, 90) * mm, "end": v(-19.32, 108) * mm});
            skLineSegment(sketch, "E80", {"start": v(-19.32, 108) * mm, "end": v(-19.32, 121.97) * mm});
            skArc(sketch, "E81", {"start": v(10.42, 121.97) * mm, "mid": v(-4.45, 135) * mm, "end": v(-19.32, 121.97) * mm});
            skLineSegment(sketch, "E82", {"start": v(10.42, 121.97) * mm, "end": v(10.42, 108) * mm});
            skLineSegment(sketch, "E83", {"start": v(10.42, 108) * mm, "end": v(28.42, 90) * mm});
            skCircle(sketch, "E84", {"center": v(-4.45, 120) * mm, "radius": 6 * mm});
            skLineSegment(sketch, "E85", {"start": v(-37.32, 90) * mm, "end": v(28.42, 90) * mm});
            skLineSegment(sketch, "E86", {"start": v(-80, 0) * mm, "end": v(80, 0) * mm, "construction": true});
            skArc(sketch, "E87.MirrorCS", {"start": v(10.42, -121.97) * mm, "mid": v(-4.45, -135) * mm, "end": v(-19.32, -121.97) * mm});
            skLineSegment(sketch, "E88.MirrorCS", {"start": v(-19.32, -108) * mm, "end": v(-19.32, -121.97) * mm});
            skLineSegment(sketch, "E89.MirrorCS", {"start": v(-37.32, -90) * mm, "end": v(-19.32, -108) * mm});
            skCircle(sketch, "E90.MirrorC", {"center": v(-4.45, -120) * mm, "radius": 6 * mm});
            skLineSegment(sketch, "E91.MirrorCS", {"start": v(10.42, -121.97) * mm, "end": v(10.42, -108) * mm});
            skLineSegment(sketch, "E92.MirrorCS", {"start": v(10.42, -108) * mm, "end": v(28.42, -90) * mm});
            skSolve(sketch);
        }
        {
            var Q0;
            Q0=makeQuery(id+"F16.imprint","IMPRINT",FACE,{"disambiguationData":[TD([[makeQuery(id+"F16.imprint","IMPRINT",EDGE,{"derivedFrom":sQuery(id+"F16.wireOp",EDGE,"E87.MirrorCS")}),-1.0]])]});
            var Q1;
            Q1=makeQuery(id+"F16.imprint","IMPRINT",FACE,{"disambiguationData":[TD([[makeQuery(id+"F16.imprint","IMPRINT",EDGE,{"derivedFrom":sQuery(id+"F16.wireOp",EDGE,"E79")}),-1.0]])]});
            var Q2;
            {var subQ5=sQuery(id+"F16.wireOp",EDGE,"E85");Q2=makeQuery(id+"F16.imprint","IMPRINT",FACE,{"disambiguationData":[TD([[makeQuery(id+"F16.imprint","IMPRINT",EDGE,{"derivedFrom":subQ5}),-1.0]])]});}
            var Q3;
            Q3=makeQuery(id+"F2.opExtrude","CAP_FACE",FACE,{"disambiguationData":[OSD([sQuery(id+"F0.wireOp",EDGE,"E12"),sQuery(id+"F0.wireOp",EDGE,"E13"),sQuery(id+"F0.wireOp",EDGE,"E14"),sQuery(id+"F0.wireOp",EDGE,"E15"),sQuery(id+"F0.wireOp",EDGE,"E17.filletArc"),sQuery(id+"F0.wireOp",EDGE,"E18.filletArc"),sQuery(id+"F0.wireOp",EDGE,"E19.filletArc"),sQuery(id+"F0.wireOp",EDGE,"E20.filletArc"),sQuery(id+"F0.wireOp",EDGE,"E25.0"),sQuery(id+"F0.wireOp",EDGE,"E25.1"),sQuery(id+"F0.wireOp",EDGE,"E25.2"),sQuery(id+"F0.wireOp",EDGE,"E25.3"),sQuery(id+"F0.wireOp",EDGE,"E25.4"),sQuery(id+"F0.wireOp",EDGE,"E25.5"),sQuery(id+"F0.wireOp",EDGE,"E25.6"),sQuery(id+"F0.wireOp",EDGE,"E25.7")])],"isStart":false});
            extrude(context, id + "F17", {"entities" : qUnion([Q0, Q1, Q2]), "endBound" : BoundingType.UP_TO_SURFACE, "depth" : 25 * mm, "endBoundEntityFace" : qUnion([Q3]), "offsetDistance" : 25 * mm});
        }
    });
